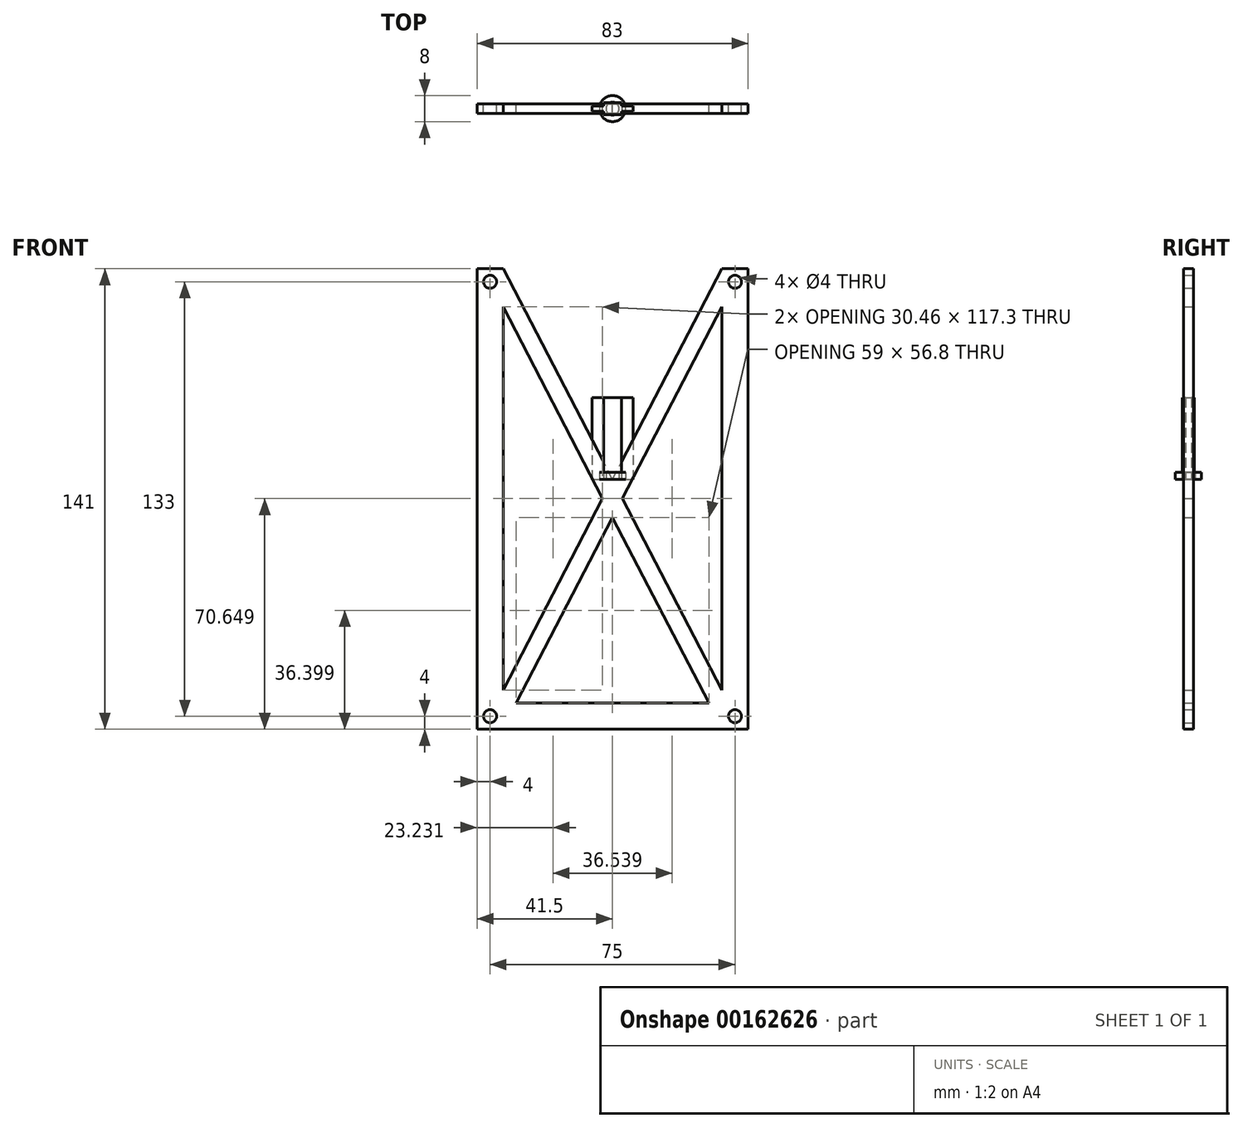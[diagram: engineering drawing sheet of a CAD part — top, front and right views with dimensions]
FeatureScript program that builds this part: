
annotation { "Feature Type Name" : "Feature", "Feature Type Description" : "" }
export const myFeature = defineFeature(function(context is Context, id is Id, definition is map)
    precondition{}
    {
        {
            var Q0;
            Q0=qCreatedBy(makeId("Top.planeOp"),FACE);
            var sketch = newSketch(context, id + "F0", { "sketchPlane" : qUnion([Q0])});
            skLineSegment(sketch, "E0", {"start": v(-6.25, -0.85) * mm, "end": v(-6.25, 0.85) * mm});
            skLineSegment(sketch, "E1", {"start": v(-6.25, 0.85) * mm, "end": v(-2.75, 0.85) * mm});
            skLineSegment(sketch, "E2", {"start": v(-2.75, 0.85) * mm, "end": v(-2.75, 1.85) * mm});
            skLineSegment(sketch, "E3", {"start": v(-2.75, 1.85) * mm, "end": v(2.75, 1.85) * mm});
            skLineSegment(sketch, "E4", {"start": v(2.75, 1.85) * mm, "end": v(2.75, 0.85) * mm});
            skLineSegment(sketch, "E5", {"start": v(2.75, 0.85) * mm, "end": v(6.25, 0.85) * mm});
            skLineSegment(sketch, "E6", {"start": v(6.25, 0.85) * mm, "end": v(6.25, -0.85) * mm});
            skLineSegment(sketch, "E7", {"start": v(-6.25, -0.85) * mm, "end": v(-2.75, -0.85) * mm});
            skLineSegment(sketch, "E8", {"start": v(-2.75, -0.85) * mm, "end": v(-2.75, -1.85) * mm});
            skLineSegment(sketch, "E9", {"start": v(-2.75, -1.85) * mm, "end": v(2.75, -1.85) * mm});
            skLineSegment(sketch, "E10", {"start": v(2.75, -1.85) * mm, "end": v(2.75, -0.85) * mm});
            skLineSegment(sketch, "E11", {"start": v(2.75, -0.85) * mm, "end": v(6.25, -0.85) * mm});
            skPoint(sketch, "E12", {"position": v(0, 0) * mm});
            skPoint(sketch, "E12.positionSnap0", {"position": v(0, 1.85) * mm});
            skPoint(sketch, "E12.positionSnap1", {"position": v(-6.25, 0) * mm});
            skSolve(sketch);
        }
        {
            var Q0;
            Q0=makeQuery(id+"F0.imprint","IMPRINT",FACE,{"disambiguationData":[TD([[makeQuery(id+"F0.imprint","IMPRINT",EDGE,{"derivedFrom":sQuery(id+"F0.wireOp",EDGE,"E0")}),-1.0]])]});
            extrude(context, id + "F1", {"entities" : qUnion([Q0]), "depth" : 25 * mm});
        }
        {
            var Q0;
            Q0=qCreatedBy(makeId("Front.planeOp"),FACE);
            var sketch = newSketch(context, id + "F2", { "sketchPlane" : qUnion([Q0])});
            skCircle(sketch, "E13", {"center": v(-37.5, 60.5) * mm, "radius": 2 * mm});
            skCircle(sketch, "E14", {"center": v(37.5, 60.5) * mm, "radius": 2 * mm});
            skCircle(sketch, "E15", {"center": v(-37.5, -72.5) * mm, "radius": 2 * mm});
            skCircle(sketch, "E16", {"center": v(37.5, -72.5) * mm, "radius": 2 * mm});
            skPoint(sketch, "E17", {"position": v(0, 0) * mm});
            skLineSegment(sketch, "E18", {"start": v(-41.5, -76.5) * mm, "end": v(41.5, -76.5) * mm});
            skLineSegment(sketch, "E19", {"start": v(41.5, -76.5) * mm, "end": v(41.5, 64.5) * mm});
            skLineSegment(sketch, "E20", {"start": v(41.5, 64.5) * mm, "end": v(33.5, 64.5) * mm});
            skLineSegment(sketch, "E21", {"start": v(33.5, 64.5) * mm, "end": v(33.5, -68.5) * mm});
            skLineSegment(sketch, "E22", {"start": v(33.5, -68.5) * mm, "end": v(-33.5, -68.5) * mm});
            skLineSegment(sketch, "E23", {"start": v(-41.5, -76.5) * mm, "end": v(-41.5, 64.5) * mm});
            skLineSegment(sketch, "E24", {"start": v(-41.5, 64.5) * mm, "end": v(-33.5, 64.5) * mm});
            skLineSegment(sketch, "E25", {"start": v(-33.5, 64.5) * mm, "end": v(-33.5, -68.5) * mm});
            skLineSegment(sketch, "E26", {"start": v(29.5, -68.5) * mm, "end": v(-33.5, 52.8) * mm});
            skLineSegment(sketch, "E27", {"start": v(33.5, -64.5) * mm, "end": v(-33.5, 64.5) * mm});
            skLineSegment(sketch, "E28", {"start": v(-29.5, -68.5) * mm, "end": v(33.5, 52.8) * mm});
            skLineSegment(sketch, "E29", {"start": v(-33.5, -64.5) * mm, "end": v(33.5, 64.5) * mm});
            skPoint(sketch, "E30", {"position": v(-37.5, 64.5) * mm});
            skLineSegment(sketch, "E31", {"start": v(-37.5, 60.5) * mm, "end": v(-37.5, 64.5) * mm, "construction": true});
            skLineSegment(sketch, "E32", {"start": v(-37.5, -72.5) * mm, "end": v(-37.5, -76.5) * mm, "construction": true});
            skLineSegment(sketch, "E33", {"start": v(37.5, -72.5) * mm, "end": v(41.5, -72.5) * mm, "construction": true});
            skLineSegment(sketch, "E34", {"start": v(-37.5, 60.5) * mm, "end": v(-41.5, 60.5) * mm, "construction": true});
            skLineSegment(sketch, "E35", {"start": v(0, -68.5) * mm, "end": v(0, -76.5) * mm, "construction": true});
            skPoint(sketch, "E36", {"position": v(0, -72.5) * mm});
            skSolve(sketch);
        }
        {
            var Q0;
            {var subQ0=sQuery(id+"F2.wireOp",EDGE,"E28");var subQ1=sQuery(id+"F2.wireOp",EDGE,"E26");var subQ2=makeQuery(id+"F2.imprint","INTERSECT",VERTEX,{"derivedFrom":[subQ1,subQ0]});Q0=makeQuery(id+"F2.imprint","IMPRINT",FACE,{"disambiguationData":[TD([[makeQuery(id+"F2.imprint","IMPRINT",EDGE,{"disambiguationData":[TD([[subQ2,-1.0]])],"derivedFrom":subQ1}),-1.0]])]});}
            var Q1;
            {var subQ1=sQuery(id+"F2.wireOp",EDGE,"E25");var subQ3=sQuery(id+"F2.wireOp",EDGE,"E26");var subQ4=makeQuery(id+"F2.imprint","INTERSECT",VERTEX,{"derivedFrom":[subQ1,subQ3]});Q1=makeQuery(id+"F2.imprint","IMPRINT",FACE,{"disambiguationData":[TD([[makeQuery(id+"F2.imprint","IMPRINT",EDGE,{"disambiguationData":[TD([[subQ4,1.0]])],"derivedFrom":subQ3}),-1.0]])]});}
            var Q2;
            {var subQ1=sQuery(id+"F2.wireOp",EDGE,"E22");var subQ3=sQuery(id+"F2.wireOp",EDGE,"E26");var subQ4=makeQuery(id+"F2.imprint","INTERSECT",VERTEX,{"derivedFrom":[subQ1,subQ3]});Q2=makeQuery(id+"F2.imprint","IMPRINT",FACE,{"disambiguationData":[TD([[makeQuery(id+"F2.imprint","IMPRINT",EDGE,{"disambiguationData":[TD([[subQ4,-1.0]])],"derivedFrom":subQ3}),-1.0]])]});}
            var Q3;
            {var subQ0=sQuery(id+"F2.wireOp",EDGE,"E29");var subQ5=sQuery(id+"F2.wireOp",EDGE,"E27");var subQ6=makeQuery(id+"F2.imprint","INTERSECT",VERTEX,{"derivedFrom":[subQ5,subQ0]});Q3=makeQuery(id+"F2.imprint","IMPRINT",FACE,{"disambiguationData":[TD([[makeQuery(id+"F2.imprint","IMPRINT",EDGE,{"disambiguationData":[TD([[subQ6,1.0]])],"derivedFrom":subQ5}),-1.0]])]});}
            var Q4;
            {var subQ3=sQuery(id+"F2.wireOp",EDGE,"E28");var subQ5=sQuery(id+"F2.wireOp",EDGE,"E26");var subQ6=makeQuery(id+"F2.imprint","INTERSECT",VERTEX,{"derivedFrom":[subQ5,subQ3]});Q4=makeQuery(id+"F2.imprint","IMPRINT",FACE,{"disambiguationData":[TD([[makeQuery(id+"F2.imprint","IMPRINT",EDGE,{"disambiguationData":[TD([[subQ6,-1.0]])],"derivedFrom":subQ5}),1.0]])]});}
            var Q5;
            Q5=makeQuery(id+"F2.imprint","IMPRINT",FACE,{"disambiguationData":[TD([[makeQuery(id+"F2.imprint","IMPRINT",EDGE,{"derivedFrom":sQuery(id+"F2.wireOp",EDGE,"E13")}),-1.0]])]});
            extrude(context, id + "F3", {"entities" : qUnion([Q0, Q1, Q2, Q3, Q4, Q5]), "endBound" : BoundingType.SYMMETRIC, "depth" : 3 * mm});
        }
        {
            var Q0;
            Q0=qCreatedBy(makeId("Top.planeOp"),FACE);
            var sketch = newSketch(context, id + "F4", { "sketchPlane" : qUnion([Q0])});
            skCircle(sketch, "E37", {"center": v(0, 0) * mm, "radius": 4 * mm});
            skCircle(sketch, "E38", {"center": v(0, 0) * mm, "radius": 2 * mm});
            skSolve(sketch);
        }
        {
            var Q0;
            Q0=makeQuery(id+"F4.imprint","IMPRINT",FACE,{"disambiguationData":[TD([[makeQuery(id+"F4.imprint","IMPRINT",EDGE,{"derivedFrom":sQuery(id+"F4.wireOp",EDGE,"E37")}),1.0]])]});
            extrude(context, id + "F5", {"entities" : qUnion([Q0]), "depth" : 2.2 * mm});
        }
    });
